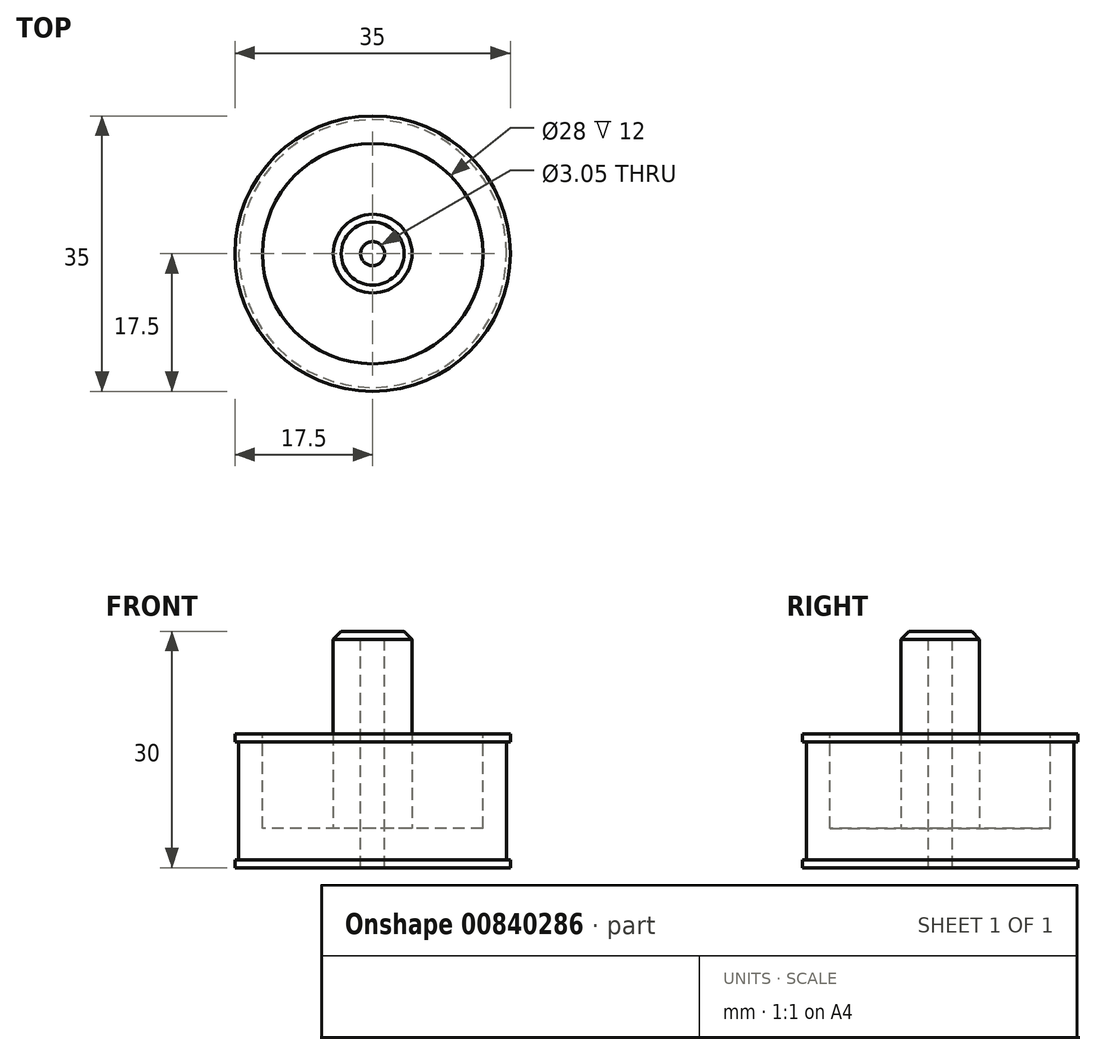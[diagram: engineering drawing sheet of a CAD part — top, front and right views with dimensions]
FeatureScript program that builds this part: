
annotation { "Feature Type Name" : "Feature", "Feature Type Description" : "" }
export const myFeature = defineFeature(function(context is Context, id is Id, definition is map)
    precondition{}
    {
        {
            var Q0;
            Q0=qCreatedBy(makeId("Top.planeOp"),FACE);
            var sketch = newSketch(context, id + "F0", { "sketchPlane" : qUnion([Q0])});
            skCircle(sketch, "E0", {"center": v(0, 0) * mm, "radius": 17.5 * mm});
            skSolve(sketch);
        }
        {
            var Q0;
            Q0 = qSketchRegion(id + "F0", true);
            extrude(context, id + "F1", {"entities" : qUnion([Q0]), "depth" : 1 * mm, "offsetDistance" : 25 * mm});
        }
        {
            var Q0;
            Q0=makeQuery(id+"F1.opExtrude","CAP_FACE",FACE,{"disambiguationData":[OSD([sQuery(id+"F0.wireOp",EDGE,"E0")])],"isStart":false});
            var sketch = newSketch(context, id + "F2", { "sketchPlane" : qUnion([Q0])});
            skCircle(sketch, "E1", {"center": v(0, 0) * mm, "radius": 17 * mm});
            skSolve(sketch);
        }
        {
            var Q0;
            Q0 = qSketchRegion(id + "F2", true);
            extrude(context, id + "F3", {"entities" : qUnion([Q0]), "operationType" : NewBodyOperationType.ADD, "depth" : 15 * mm, "offsetDistance" : 25 * mm});
        }
        {
            var Q0;
            Q0=makeQuery(id+"F3.opExtrude","CAP_FACE",FACE,{"disambiguationData":[OSD([sQuery(id+"F2.wireOp",EDGE,"E1")])],"isStart":false});
            var sketch = newSketch(context, id + "F4", { "sketchPlane" : qUnion([Q0])});
            skCircle(sketch, "E2", {"center": v(0, 0) * mm, "radius": 17.5 * mm});
            skSolve(sketch);
        }
        {
            var Q0;
            Q0 = qSketchRegion(id + "F4", true);
            extrude(context, id + "F5", {"entities" : qUnion([Q0]), "operationType" : NewBodyOperationType.ADD, "depth" : 1 * mm, "offsetDistance" : 25 * mm});
        }
        {
            var Q0;
            Q0=makeQuery(id+"F5.opExtrude","CAP_FACE",FACE,{"disambiguationData":[OSD([sQuery(id+"F4.wireOp",EDGE,"E2")])],"isStart":false});
            var sketch = newSketch(context, id + "F6", { "sketchPlane" : qUnion([Q0])});
            skCircle(sketch, "E3", {"center": v(0, 0) * mm, "radius": 14 * mm});
            skSolve(sketch);
        }
        {
            var Q0;
            Q0 = qSketchRegion(id + "F6", true);
            extrude(context, id + "F7", {"entities" : qUnion([Q0]), "operationType" : NewBodyOperationType.REMOVE, "oppositeDirection" : true, "depth" : 12 * mm, "offsetDistance" : 25 * mm});
        }
        {
            var Q0;
            Q0=makeQuery(id+"F7.boolean.opBoolean","COPY",FACE,{"derivedFrom":makeQuery(id+"F7.opExtrude","CAP_FACE",FACE,{"disambiguationData":[OSD([sQuery(id+"F6.wireOp",EDGE,"E3")])],"isStart":false})});
            var sketch = newSketch(context, id + "F8", { "sketchPlane" : qUnion([Q0])});
            skCircle(sketch, "E4", {"center": v(0, 0) * mm, "radius": 5 * mm});
            skSolve(sketch);
        }
        {
            var Q0;
            Q0 = qSketchRegion(id + "F8", true);
            extrude(context, id + "F9", {"entities" : qUnion([Q0]), "operationType" : NewBodyOperationType.ADD, "depth" : 25 * mm, "offsetDistance" : 25 * mm});
        }
        {
            var Q0;
            Q0=makeQuery(id+"F9.opExtrude","CAP_FACE",FACE,{"disambiguationData":[OSD([sQuery(id+"F8.wireOp",EDGE,"E4")])],"isStart":false});
            var sketch = newSketch(context, id + "F10", { "sketchPlane" : qUnion([Q0])});
            skCircle(sketch, "E5", {"center": v(0, 0) * mm, "radius": 1.52 * mm});
            skSolve(sketch);
        }
        {
            var Q0;
            Q0 = qSketchRegion(id + "F10", true);
            extrude(context, id + "F11", {"entities" : qUnion([Q0]), "operationType" : NewBodyOperationType.REMOVE, "endBound" : BoundingType.UP_TO_NEXT, "oppositeDirection" : true, "depth" : -8 * mm, "offsetDistance" : 25 * mm});
        }
        {
            var Q0;
            Q0=makeQuery(id+"F11.boolean.opBoolean","COPY",EDGE,{"derivedFrom":makeQuery(id+"F11.opExtrude","CAP_EDGE",EDGE,{"disambiguationData":[OSD([sQuery(id+"F10.wireOp",EDGE,"E5")])],"isStart":true})});
            var Q1;
            Q1=makeQuery(id+"F9.opExtrude","CAP_EDGE",EDGE,{"disambiguationData":[OSD([sQuery(id+"F8.wireOp",EDGE,"E4")])],"isStart":false});
            chamfer(context, id + "F12", {"entities" : qUnion([Q0, Q1]), "width" : 1 * mm, "tangentPropagation" : true});
        }
    });
